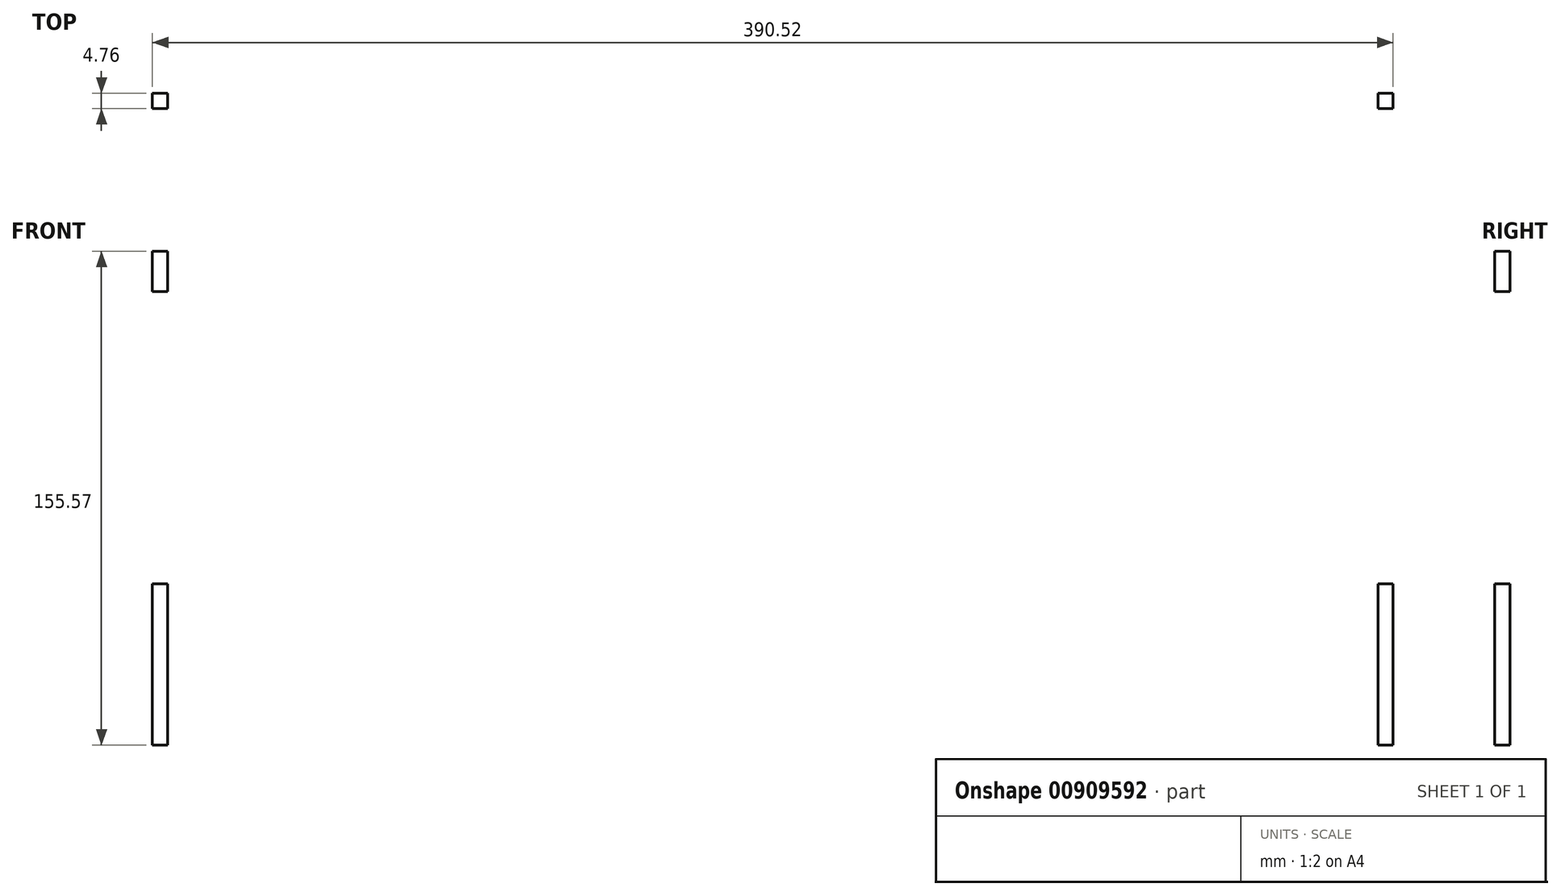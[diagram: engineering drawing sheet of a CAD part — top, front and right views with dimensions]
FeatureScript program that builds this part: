
annotation { "Feature Type Name" : "Feature", "Feature Type Description" : "" }
export const myFeature = defineFeature(function(context is Context, id is Id, definition is map)
    precondition{}
    {
        {
            var Q0;
            Q0=qCreatedBy(makeId("Front.planeOp"),FACE);
            var sketch = newSketch(context, id + "F0", { "sketchPlane" : qUnion([Q0])});
            skLineSegment(sketch, "E0.bottom", {"start": v(-195.26, 88.9) * mm, "end": v(195.26, 88.9) * mm});
            skLineSegment(sketch, "E0.top", {"start": v(-195.26, -88.9) * mm, "end": v(195.26, -88.9) * mm});
            skLineSegment(sketch, "E0.left", {"start": v(-195.26, 88.9) * mm, "end": v(-195.26, -88.9) * mm});
            skLineSegment(sketch, "E0.right", {"start": v(195.26, 88.9) * mm, "end": v(195.26, -88.9) * mm});
            skPoint(sketch, "E0.middle", {"position": v(0, 0) * mm});
            skLineSegment(sketch, "E1.0", {"start": v(-190.5, 88.9) * mm, "end": v(-190.5, -88.9) * mm});
            skLineSegment(sketch, "E2.0", {"start": v(190.5, 88.9) * mm, "end": v(190.5, -88.9) * mm});
            skLineSegment(sketch, "E3.bottom", {"start": v(-127, 31.75) * mm, "end": v(-76.2, 31.75) * mm});
            skLineSegment(sketch, "E3.top", {"start": v(-127, 25.4) * mm, "end": v(-76.2, 25.4) * mm});
            skLineSegment(sketch, "E3.left", {"start": v(-127, 31.75) * mm, "end": v(-127, 25.4) * mm});
            skLineSegment(sketch, "E3.right", {"start": v(-76.2, 31.75) * mm, "end": v(-76.2, 25.4) * mm});
            skLineSegment(sketch, "E4.0", {"start": v(-127.13, 31.88) * mm, "end": v(-76.07, 31.88) * mm});
            skLineSegment(sketch, "E4.1", {"start": v(-127.13, 31.88) * mm, "end": v(-127.13, 25.27) * mm});
            skLineSegment(sketch, "E4.2", {"start": v(-127.13, 25.27) * mm, "end": v(-76.07, 25.27) * mm});
            skLineSegment(sketch, "E4.3", {"start": v(-76.07, 31.88) * mm, "end": v(-76.07, 25.27) * mm});
            skLineSegment(sketch, "E5.1.0.0", {"start": v(-25.53, 31.88) * mm, "end": v(-25.53, 25.27) * mm});
            skLineSegment(sketch, "E5.1.0.1", {"start": v(-25.53, 31.88) * mm, "end": v(25.53, 31.88) * mm});
            skLineSegment(sketch, "E5.1.0.2", {"start": v(-25.53, 25.27) * mm, "end": v(25.53, 25.27) * mm});
            skLineSegment(sketch, "E5.1.0.3", {"start": v(25.4, 31.75) * mm, "end": v(25.4, 25.4) * mm});
            skLineSegment(sketch, "E5.1.0.4", {"start": v(-25.4, 31.75) * mm, "end": v(25.4, 31.75) * mm});
            skLineSegment(sketch, "E5.1.0.5", {"start": v(25.53, 31.88) * mm, "end": v(25.53, 25.27) * mm});
            skLineSegment(sketch, "E5.1.0.6", {"start": v(-25.4, 31.75) * mm, "end": v(-25.4, 25.4) * mm});
            skLineSegment(sketch, "E5.1.0.7", {"start": v(-25.4, 25.4) * mm, "end": v(25.4, 25.4) * mm});
            skLineSegment(sketch, "E5.2.0.0", {"start": v(76.07, 31.88) * mm, "end": v(76.07, 25.27) * mm});
            skLineSegment(sketch, "E5.2.0.1", {"start": v(76.07, 31.88) * mm, "end": v(127.13, 31.88) * mm});
            skLineSegment(sketch, "E5.2.0.2", {"start": v(76.07, 25.27) * mm, "end": v(127.13, 25.27) * mm});
            skLineSegment(sketch, "E5.2.0.3", {"start": v(127, 31.75) * mm, "end": v(127, 25.4) * mm});
            skLineSegment(sketch, "E5.2.0.4", {"start": v(76.2, 31.75) * mm, "end": v(127, 31.75) * mm});
            skLineSegment(sketch, "E5.2.0.5", {"start": v(127.13, 31.88) * mm, "end": v(127.13, 25.27) * mm});
            skLineSegment(sketch, "E5.2.0.6", {"start": v(76.2, 31.75) * mm, "end": v(76.2, 25.4) * mm});
            skLineSegment(sketch, "E5.2.0.7", {"start": v(76.2, 25.4) * mm, "end": v(127, 25.4) * mm});
            skLineSegment(sketch, "E5.direction1", {"start": v(-127, 25.4) * mm, "end": v(-25.4, 25.4) * mm, "construction": true});
            skLineSegment(sketch, "E6.bottom", {"start": v(-195.26, -88.9) * mm, "end": v(-190.5, -88.9) * mm});
            skLineSegment(sketch, "E6.top", {"start": v(-195.26, -38.1) * mm, "end": v(-190.5, -38.1) * mm});
            skLineSegment(sketch, "E6.left", {"start": v(-195.26, -88.9) * mm, "end": v(-195.26, -38.1) * mm});
            skLineSegment(sketch, "E6.right", {"start": v(-190.5, -88.9) * mm, "end": v(-190.5, -38.1) * mm});
            skLineSegment(sketch, "E7", {"start": v(0, 88.9) * mm, "end": v(0, -88.9) * mm, "construction": true});
            skLineSegment(sketch, "E8.MirrorCS", {"start": v(195.26, -88.9) * mm, "end": v(190.5, -88.9) * mm});
            skLineSegment(sketch, "E9.MirrorCS", {"start": v(195.26, -38.1) * mm, "end": v(190.5, -38.1) * mm});
            skLineSegment(sketch, "E10.MirrorCS", {"start": v(195.26, -88.9) * mm, "end": v(195.26, -38.1) * mm});
            skLineSegment(sketch, "E11.MirrorCS", {"start": v(190.5, -88.9) * mm, "end": v(190.5, -38.1) * mm});
            skLineSegment(sketch, "E12.bottom", {"start": v(-127, 88.9) * mm, "end": v(-76.2, 88.9) * mm});
            skLineSegment(sketch, "E12.top", {"start": v(-127, 93.66) * mm, "end": v(-76.2, 93.66) * mm});
            skLineSegment(sketch, "E12.left", {"start": v(-127, 88.9) * mm, "end": v(-127, 93.66) * mm});
            skLineSegment(sketch, "E12.right", {"start": v(-76.2, 88.9) * mm, "end": v(-76.2, 93.66) * mm});
            skLineSegment(sketch, "E13.1.0.0", {"start": v(-25.4, 88.9) * mm, "end": v(25.4, 88.9) * mm});
            skLineSegment(sketch, "E13.1.0.1", {"start": v(25.4, 88.9) * mm, "end": v(25.4, 93.66) * mm});
            skLineSegment(sketch, "E13.1.0.2", {"start": v(-25.4, 93.66) * mm, "end": v(25.4, 93.66) * mm});
            skLineSegment(sketch, "E13.1.0.3", {"start": v(-25.4, 88.9) * mm, "end": v(-25.4, 93.66) * mm});
            skLineSegment(sketch, "E13.2.0.0", {"start": v(76.2, 88.9) * mm, "end": v(127, 88.9) * mm});
            skLineSegment(sketch, "E13.2.0.1", {"start": v(127, 88.9) * mm, "end": v(127, 93.66) * mm});
            skLineSegment(sketch, "E13.2.0.2", {"start": v(76.2, 93.66) * mm, "end": v(127, 93.66) * mm});
            skLineSegment(sketch, "E13.2.0.3", {"start": v(76.2, 88.9) * mm, "end": v(76.2, 93.66) * mm});
            skLineSegment(sketch, "E13.direction1", {"start": v(-127, 88.9) * mm, "end": v(-25.4, 88.9) * mm, "construction": true});
            skLineSegment(sketch, "E14.bottom", {"start": v(-190.5, 46.3) * mm, "end": v(-171.45, 46.3) * mm});
            skLineSegment(sketch, "E14.top", {"start": v(-190.5, 42.6) * mm, "end": v(-171.45, 42.6) * mm});
            skLineSegment(sketch, "E14.left", {"start": v(-190.5, 46.3) * mm, "end": v(-190.5, 42.6) * mm});
            skLineSegment(sketch, "E14.right", {"start": v(-171.45, 46.3) * mm, "end": v(-171.45, 42.6) * mm});
            skPoint(sketch, "E15", {"position": v(-190.5, 44.45) * mm});
            skLineSegment(sketch, "E16.bottom", {"start": v(-182.56, 48.58) * mm, "end": v(-179.39, 48.58) * mm});
            skLineSegment(sketch, "E16.top", {"start": v(-182.56, 40.32) * mm, "end": v(-179.39, 40.32) * mm});
            skLineSegment(sketch, "E16.left", {"start": v(-182.56, 48.58) * mm, "end": v(-182.56, 40.32) * mm});
            skLineSegment(sketch, "E16.right", {"start": v(-179.39, 48.58) * mm, "end": v(-179.39, 40.32) * mm});
            skPoint(sketch, "E17", {"position": v(-179.39, 44.45) * mm});
            skLineSegment(sketch, "E18", {"start": v(-190.5, 44.45) * mm, "end": v(-171.45, 44.45) * mm, "construction": true});
            skLineSegment(sketch, "E19", {"start": v(-180.97, 48.58) * mm, "end": v(-180.97, 40.32) * mm, "construction": true});
            skLineSegment(sketch, "E20.bottom", {"start": v(-190.5, 66.68) * mm, "end": v(-195.26, 66.68) * mm});
            skLineSegment(sketch, "E20.top", {"start": v(-190.5, 53.98) * mm, "end": v(-195.26, 53.98) * mm});
            skLineSegment(sketch, "E20.left", {"start": v(-190.5, 66.68) * mm, "end": v(-190.5, 53.98) * mm});
            skLineSegment(sketch, "E20.right", {"start": v(-195.26, 66.68) * mm, "end": v(-195.26, 53.98) * mm});
            skPoint(sketch, "E21", {"position": v(-190.5, 60.33) * mm});
            skPoint(sketch, "E22.MirrorP", {"position": v(-190.5, 28.58) * mm});
            skLineSegment(sketch, "E23.MirrorCS", {"start": v(-195.26, 22.23) * mm, "end": v(-195.26, 34.93) * mm});
            skLineSegment(sketch, "E24.MirrorCS", {"start": v(-190.5, 22.23) * mm, "end": v(-195.26, 22.23) * mm});
            skLineSegment(sketch, "E25.MirrorCS", {"start": v(-190.5, 34.93) * mm, "end": v(-195.26, 34.93) * mm});
            skLineSegment(sketch, "E26.MirrorCS", {"start": v(-190.5, 22.23) * mm, "end": v(-190.5, 34.93) * mm});
            skLineSegment(sketch, "E27.MirrorCS", {"start": v(190.5, 46.3) * mm, "end": v(190.5, 42.6) * mm});
            skPoint(sketch, "E28.MirrorP", {"position": v(190.5, 60.32) * mm});
            skLineSegment(sketch, "E29.MirrorCS", {"start": v(195.26, 66.68) * mm, "end": v(195.26, 53.97) * mm});
            skLineSegment(sketch, "E30.MirrorCS", {"start": v(190.5, 66.68) * mm, "end": v(195.26, 66.68) * mm});
            skPoint(sketch, "E31.MirrorP", {"position": v(190.5, 28.58) * mm});
            skLineSegment(sketch, "E32.MirrorCS", {"start": v(195.26, 22.22) * mm, "end": v(195.26, 34.93) * mm});
            skLineSegment(sketch, "E33.MirrorCS", {"start": v(190.5, 34.93) * mm, "end": v(195.26, 34.93) * mm});
            skLineSegment(sketch, "E34.MirrorCS", {"start": v(190.5, 53.98) * mm, "end": v(195.26, 53.98) * mm});
            skPoint(sketch, "E35.MirrorP", {"position": v(190.5, 44.45) * mm});
            skLineSegment(sketch, "E36.MirrorCS", {"start": v(190.5, 22.23) * mm, "end": v(190.5, 34.92) * mm});
            skLineSegment(sketch, "E37.MirrorCS", {"start": v(190.5, 66.67) * mm, "end": v(190.5, 53.98) * mm});
            skLineSegment(sketch, "E38.MirrorCS", {"start": v(190.5, 22.23) * mm, "end": v(195.26, 22.23) * mm});
            skLineSegment(sketch, "E39.MirrorCS", {"start": v(171.45, 46.3) * mm, "end": v(171.45, 42.6) * mm});
            skLineSegment(sketch, "E40.MirrorCS", {"start": v(182.56, 40.32) * mm, "end": v(179.39, 40.32) * mm});
            skLineSegment(sketch, "E41.MirrorCS", {"start": v(182.56, 48.58) * mm, "end": v(179.39, 48.58) * mm});
            skLineSegment(sketch, "E42.MirrorCS", {"start": v(180.98, 48.58) * mm, "end": v(180.98, 40.32) * mm, "construction": true});
            skLineSegment(sketch, "E43.MirrorCS", {"start": v(179.39, 48.58) * mm, "end": v(179.39, 40.32) * mm});
            skLineSegment(sketch, "E44.MirrorCS", {"start": v(190.5, 44.45) * mm, "end": v(171.45, 44.45) * mm, "construction": true});
            skLineSegment(sketch, "E45.MirrorCS", {"start": v(190.5, 46.3) * mm, "end": v(171.45, 46.3) * mm});
            skLineSegment(sketch, "E46.MirrorCS", {"start": v(182.56, 48.58) * mm, "end": v(182.56, 40.32) * mm});
            skPoint(sketch, "E47.MirrorP", {"position": v(179.39, 44.45) * mm});
            skLineSegment(sketch, "E48.MirrorCS", {"start": v(190.5, 42.6) * mm, "end": v(171.45, 42.6) * mm});
            skLineSegment(sketch, "E49.bottom", {"start": v(-52.64, 88.9) * mm, "end": v(-48.96, 88.9) * mm});
            skLineSegment(sketch, "E49.top", {"start": v(-52.64, 69.85) * mm, "end": v(-48.96, 69.85) * mm});
            skLineSegment(sketch, "E49.left", {"start": v(-52.64, 88.9) * mm, "end": v(-52.64, 69.85) * mm});
            skLineSegment(sketch, "E49.right", {"start": v(-48.96, 88.9) * mm, "end": v(-48.96, 69.85) * mm});
            skLineSegment(sketch, "E50", {"start": v(-50.8, 88.9) * mm, "end": v(-50.8, 69.85) * mm, "construction": true});
            skPoint(sketch, "E51", {"position": v(-50.8, 88.9) * mm});
            skLineSegment(sketch, "E52.bottom", {"start": v(-54.93, 79.38) * mm, "end": v(-46.67, 79.38) * mm});
            skLineSegment(sketch, "E52.top", {"start": v(-54.93, 76.2) * mm, "end": v(-46.67, 76.2) * mm});
            skLineSegment(sketch, "E52.left", {"start": v(-54.93, 79.37) * mm, "end": v(-54.93, 76.2) * mm});
            skLineSegment(sketch, "E52.right", {"start": v(-46.67, 79.37) * mm, "end": v(-46.67, 76.2) * mm});
            skLineSegment(sketch, "E53", {"start": v(-54.93, 77.79) * mm, "end": v(-46.67, 77.79) * mm, "construction": true});
            skPoint(sketch, "E54", {"position": v(-50.8, 76.2) * mm});
            skLineSegment(sketch, "E55.MirrorCS", {"start": v(52.64, 88.9) * mm, "end": v(48.96, 88.9) * mm});
            skLineSegment(sketch, "E56.MirrorCS", {"start": v(54.93, 79.37) * mm, "end": v(54.93, 76.2) * mm});
            skLineSegment(sketch, "E57.MirrorCS", {"start": v(46.67, 79.37) * mm, "end": v(46.67, 76.2) * mm});
            skLineSegment(sketch, "E58.MirrorCS", {"start": v(52.64, 69.85) * mm, "end": v(48.96, 69.85) * mm});
            skLineSegment(sketch, "E59.MirrorCS", {"start": v(54.93, 77.79) * mm, "end": v(46.67, 77.79) * mm, "construction": true});
            skLineSegment(sketch, "E60.MirrorCS", {"start": v(54.93, 76.2) * mm, "end": v(46.67, 76.2) * mm});
            skPoint(sketch, "E61.MirrorP", {"position": v(50.8, 88.9) * mm});
            skLineSegment(sketch, "E62.MirrorCS", {"start": v(48.96, 88.9) * mm, "end": v(48.96, 69.85) * mm});
            skLineSegment(sketch, "E63.MirrorCS", {"start": v(54.93, 79.38) * mm, "end": v(46.67, 79.38) * mm});
            skLineSegment(sketch, "E64.MirrorCS", {"start": v(50.8, 88.9) * mm, "end": v(50.8, 69.85) * mm, "construction": true});
            skPoint(sketch, "E65.MirrorP", {"position": v(50.8, 76.2) * mm});
            skLineSegment(sketch, "E66.MirrorCS", {"start": v(52.64, 88.9) * mm, "end": v(52.64, 69.85) * mm});
            skCircle(sketch, "E67", {"center": v(75.07, -46.92) * mm, "radius": 1.59 * mm});
            skCircle(sketch, "E68", {"center": v(75.07, -71.92) * mm, "radius": 1.59 * mm});
            skCircle(sketch, "E69", {"center": v(-74.93, -46.92) * mm, "radius": 1.59 * mm});
            skCircle(sketch, "E70", {"center": v(-74.93, -71.92) * mm, "radius": 1.59 * mm});
            skLineSegment(sketch, "E71", {"start": v(-190.5, 28.58) * mm, "end": v(-127, 28.58) * mm, "construction": true});
            skLineSegment(sketch, "E72", {"start": v(-76.07, 28.58) * mm, "end": v(-25.4, 28.58) * mm, "construction": true});
            skLineSegment(sketch, "E73", {"start": v(25.4, 28.58) * mm, "end": v(76.2, 28.58) * mm, "construction": true});
            skLineSegment(sketch, "E74", {"start": v(127, 28.58) * mm, "end": v(190.5, 28.58) * mm, "construction": true});
            skCircle(sketch, "E75", {"center": v(-158.75, 28.58) * mm, "radius": 1.84 * mm, "construction": true});
            skCircle(sketch, "E76", {"center": v(-50.74, 28.58) * mm, "radius": 1.84 * mm, "construction": true});
            skCircle(sketch, "E77", {"center": v(50.8, 28.58) * mm, "radius": 1.84 * mm, "construction": true});
            skCircle(sketch, "E78", {"center": v(158.75, 28.58) * mm, "radius": 1.84 * mm, "construction": true});
            skSolve(sketch);
        }
        {
            var Q0;
            Q0=makeQuery(id+"F0.imprint","IMPRINT",FACE,{"disambiguationData":[TD([[makeQuery(id+"F0.imprint","IMPRINT",EDGE,{"derivedFrom":sQuery(id+"F0.wireOp",EDGE,"E0.top")}),1.0]])]});
            var Q1;
            Q1=makeQuery(id+"F0.imprint","IMPRINT",FACE,{"disambiguationData":[TD([[makeQuery(id+"F0.imprint","IMPRINT",EDGE,{"derivedFrom":sQuery(id+"F0.wireOp",EDGE,"E8.MirrorCS")}),-1.0]])]});
            var Q2;
            Q2=makeQuery(id+"F0.imprint","IMPRINT",FACE,{"disambiguationData":[TD([[makeQuery(id+"F0.imprint","IMPRINT",EDGE,{"derivedFrom":sQuery(id+"F0.wireOp",EDGE,"E6.bottom")}),1.0]])]});
            var Q3;
            Q3=makeQuery(id+"F0.imprint","IMPRINT",FACE,{"disambiguationData":[TD([[makeQuery(id+"F0.imprint","IMPRINT",EDGE,{"derivedFrom":sQuery(id+"F0.wireOp",EDGE,"E12.bottom")}),1.0]])]});
            var Q4;
            Q4=makeQuery(id+"F0.imprint","IMPRINT",FACE,{"disambiguationData":[TD([[makeQuery(id+"F0.imprint","IMPRINT",EDGE,{"derivedFrom":sQuery(id+"F0.wireOp",EDGE,"E13.1.0.0")}),1.0]])]});
            var Q5;
            Q5=makeQuery(id+"F0.imprint","IMPRINT",FACE,{"disambiguationData":[TD([[makeQuery(id+"F0.imprint","IMPRINT",EDGE,{"derivedFrom":sQuery(id+"F0.wireOp",EDGE,"E13.2.0.0")}),1.0]])]});
            var Q6;
            Q6=makeQuery(id+"F0.imprint","IMPRINT",FACE,{"disambiguationData":[TD([[makeQuery(id+"F0.imprint","IMPRINT",EDGE,{"derivedFrom":sQuery(id+"F0.wireOp",EDGE,"E20.bottom")}),1.0]])]});
            var Q7;
            Q7=makeQuery(id+"F0.imprint","IMPRINT",FACE,{"disambiguationData":[TD([[makeQuery(id+"F0.imprint","IMPRINT",EDGE,{"derivedFrom":sQuery(id+"F0.wireOp",EDGE,"E23.MirrorCS")}),-1.0]])]});
            extrude(context, id + "F1", {"entities" : qUnion([Q0, Q1, Q2, Q3, Q4, Q5, Q6, Q7]), "depth" : 4.76 * mm, "offsetDistance" : 25.4 * mm});
        }
        {
            var Q0;
            Q0=sQuery(id+"F0.wireOp",VERTEX,"E75.center");
            var Q1;
            Q1=sQuery(id+"F0.wireOp",VERTEX,"E76.center");
            var Q2;
            Q2=sQuery(id+"F0.wireOp",VERTEX,"E77.center");
            var Q3;
            Q3=sQuery(id+"F0.wireOp",VERTEX,"E78.center");
            var Q4;
            Q4=makeQuery(id+"F1.opExtrude","SWEPT_BODY",BODY,{"disambiguationData":[OSD([sQuery(id+"F0.wireOp",EDGE,"E0.bottom"),sQuery(id+"F0.wireOp",EDGE,"E0.top"),sQuery(id+"F0.wireOp",EDGE,"E1.0"),sQuery(id+"F0.wireOp",EDGE,"E2.0"),sQuery(id+"F0.wireOp",EDGE,"E4.0"),sQuery(id+"F0.wireOp",EDGE,"E4.1"),sQuery(id+"F0.wireOp",EDGE,"E4.2"),sQuery(id+"F0.wireOp",EDGE,"E4.3"),sQuery(id+"F0.wireOp",EDGE,"E5.1.0.0"),sQuery(id+"F0.wireOp",EDGE,"E5.1.0.1"),sQuery(id+"F0.wireOp",EDGE,"E5.1.0.2"),sQuery(id+"F0.wireOp",EDGE,"E5.1.0.5"),sQuery(id+"F0.wireOp",EDGE,"E5.2.0.0"),sQuery(id+"F0.wireOp",EDGE,"E5.2.0.1"),sQuery(id+"F0.wireOp",EDGE,"E5.2.0.2"),sQuery(id+"F0.wireOp",EDGE,"E5.2.0.5"),sQuery(id+"F0.wireOp",EDGE,"E8.MirrorCS"),sQuery(id+"F0.wireOp",EDGE,"E9.MirrorCS"),sQuery(id+"F0.wireOp",EDGE,"E10.MirrorCS"),sQuery(id+"F0.wireOp",EDGE,"E6.bottom"),sQuery(id+"F0.wireOp",EDGE,"E6.left"),sQuery(id+"F0.wireOp",EDGE,"E6.top"),sQuery(id+"F0.wireOp",EDGE,"E12.top"),sQuery(id+"F0.wireOp",EDGE,"E12.left"),sQuery(id+"F0.wireOp",EDGE,"E12.right"),sQuery(id+"F0.wireOp",EDGE,"E13.1.0.1"),sQuery(id+"F0.wireOp",EDGE,"E13.1.0.2"),sQuery(id+"F0.wireOp",EDGE,"E13.1.0.3"),sQuery(id+"F0.wireOp",EDGE,"E13.2.0.1"),sQuery(id+"F0.wireOp",EDGE,"E13.2.0.2"),sQuery(id+"F0.wireOp",EDGE,"E13.2.0.3"),sQuery(id+"F0.wireOp",EDGE,"E14.bottom"),sQuery(id+"F0.wireOp",EDGE,"E14.top"),sQuery(id+"F0.wireOp",EDGE,"E14.right"),sQuery(id+"F0.wireOp",EDGE,"E16.bottom"),sQuery(id+"F0.wireOp",EDGE,"E16.top"),sQuery(id+"F0.wireOp",EDGE,"E16.left"),sQuery(id+"F0.wireOp",EDGE,"E16.right"),sQuery(id+"F0.wireOp",EDGE,"E20.bottom"),sQuery(id+"F0.wireOp",EDGE,"E20.top"),sQuery(id+"F0.wireOp",EDGE,"E20.right"),sQuery(id+"F0.wireOp",EDGE,"E23.MirrorCS"),sQuery(id+"F0.wireOp",EDGE,"E24.MirrorCS"),sQuery(id+"F0.wireOp",EDGE,"E25.MirrorCS"),sQuery(id+"F0.wireOp",EDGE,"E36.MirrorCS"),sQuery(id+"F0.wireOp",EDGE,"E37.MirrorCS"),sQuery(id+"F0.wireOp",EDGE,"E39.MirrorCS"),sQuery(id+"F0.wireOp",EDGE,"E40.MirrorCS"),sQuery(id+"F0.wireOp",EDGE,"E41.MirrorCS"),sQuery(id+"F0.wireOp",EDGE,"E43.MirrorCS"),sQuery(id+"F0.wireOp",EDGE,"E45.MirrorCS"),sQuery(id+"F0.wireOp",EDGE,"E46.MirrorCS"),sQuery(id+"F0.wireOp",EDGE,"E48.MirrorCS"),sQuery(id+"F0.wireOp",EDGE,"E49.top"),sQuery(id+"F0.wireOp",EDGE,"E49.left"),sQuery(id+"F0.wireOp",EDGE,"E49.right"),sQuery(id+"F0.wireOp",EDGE,"E52.bottom"),sQuery(id+"F0.wireOp",EDGE,"E52.top"),sQuery(id+"F0.wireOp",EDGE,"E52.left"),sQuery(id+"F0.wireOp",EDGE,"E52.right"),sQuery(id+"F0.wireOp",EDGE,"E56.MirrorCS"),sQuery(id+"F0.wireOp",EDGE,"E57.MirrorCS"),sQuery(id+"F0.wireOp",EDGE,"E58.MirrorCS"),sQuery(id+"F0.wireOp",EDGE,"E60.MirrorCS"),sQuery(id+"F0.wireOp",EDGE,"E62.MirrorCS"),sQuery(id+"F0.wireOp",EDGE,"E63.MirrorCS"),sQuery(id+"F0.wireOp",EDGE,"E66.MirrorCS"),sQuery(id+"F0.wireOp",EDGE,"E67"),sQuery(id+"F0.wireOp",EDGE,"E68"),sQuery(id+"F0.wireOp",EDGE,"E69"),sQuery(id+"F0.wireOp",EDGE,"E70")])]});
            hole(context, id + "F2", {"style" : HoleStyle.SIMPLE, "endStyle" : HoleEndStyle.BLIND, "oppositeDirection" : true, "standardTappedOrClearance" : lookupTablePath({ "fit" : "Normal (ASME)", "standard" : "ANSI", "size" : "#6", "type" : "Clearance" }), "standardBlindInLast" : lookupTablePath({ "fit" : "Normal", "standard" : "ANSI", "size" : "#6", "type" : "Clearance" }), "holeDiameter" : 4.32 * mm, "majorDiameter" : 3.5 * mm, "holeDepth" : 11.9 * mm, "isTappedThrough" : true, "tappedDepth" : 9.53 * mm, "tapClearance" : 3, "locations" : qUnion([Q0, Q1, Q2, Q3]), "scope" : qUnion([Q4])});
        }
    });
